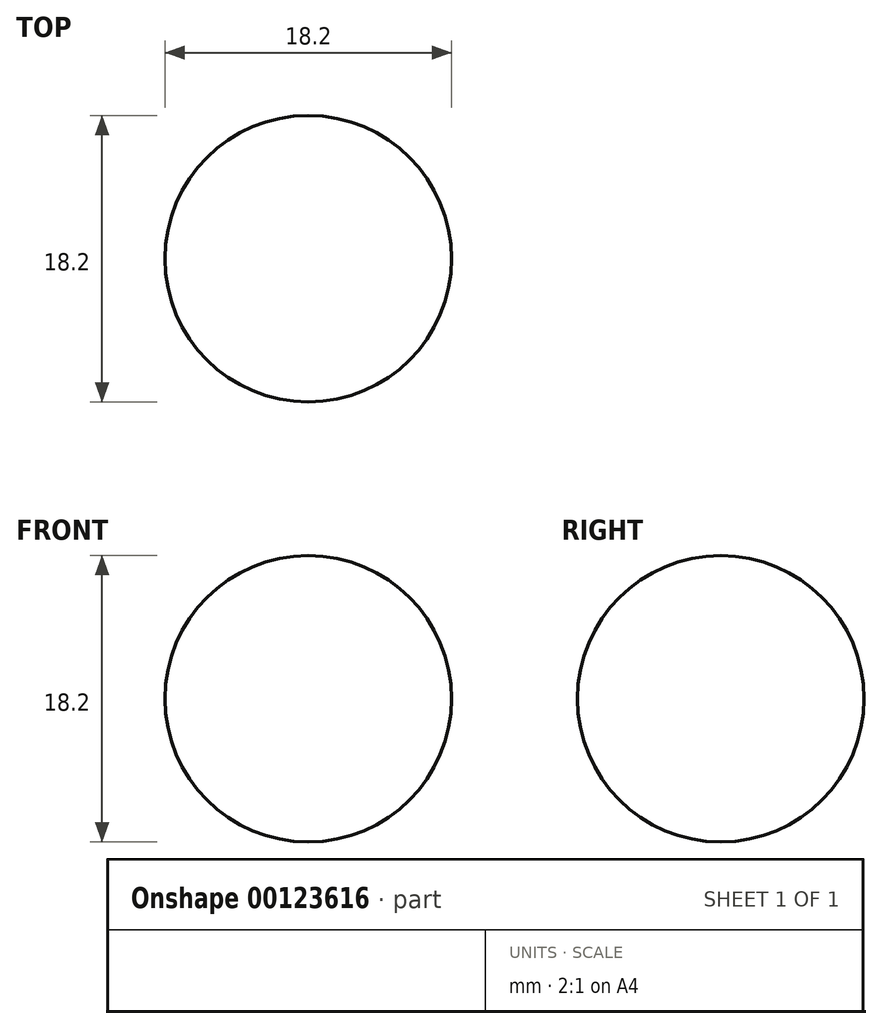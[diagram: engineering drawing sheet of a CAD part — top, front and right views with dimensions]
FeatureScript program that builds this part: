
annotation { "Feature Type Name" : "Feature", "Feature Type Description" : "" }
export const myFeature = defineFeature(function(context is Context, id is Id, definition is map)
    precondition{}
    {
        {
            var Q0;
            Q0=qCreatedBy(makeId("Front.planeOp"),FACE);
            var sketch = newSketch(context, id + "F0", { "sketchPlane" : qUnion([Q0])});
            skArc(sketch, "E0", {"start": v(0, -9.1) * mm, "mid": v(9.1, 0) * mm, "end": v(0, 9.1) * mm});
            skLineSegment(sketch, "E1", {"start": v(0, 9.1) * mm, "end": v(0, 44.64) * mm});
            skLineSegment(sketch, "E2", {"start": v(0, 9.1) * mm, "end": v(0, -9.1) * mm});
            skSolve(sketch);
        }
        {
            var Q0;
            Q0=makeQuery(id+"F0.imprint","IMPRINT",FACE,{"disambiguationData":[TD([[makeQuery(id+"F0.imprint","IMPRINT",EDGE,{"derivedFrom":sQuery(id+"F0.wireOp",EDGE,"E0")}),1.0]])]});
            var Q1;
            Q1=sQuery(id+"F0.wireOp",EDGE,"E1");
            revolve(context, id + "F1", {"entities" : qUnion([Q0]), "axis" : qUnion([Q1]), "revolveType" : RevolveType.FULL});
        }
    });
